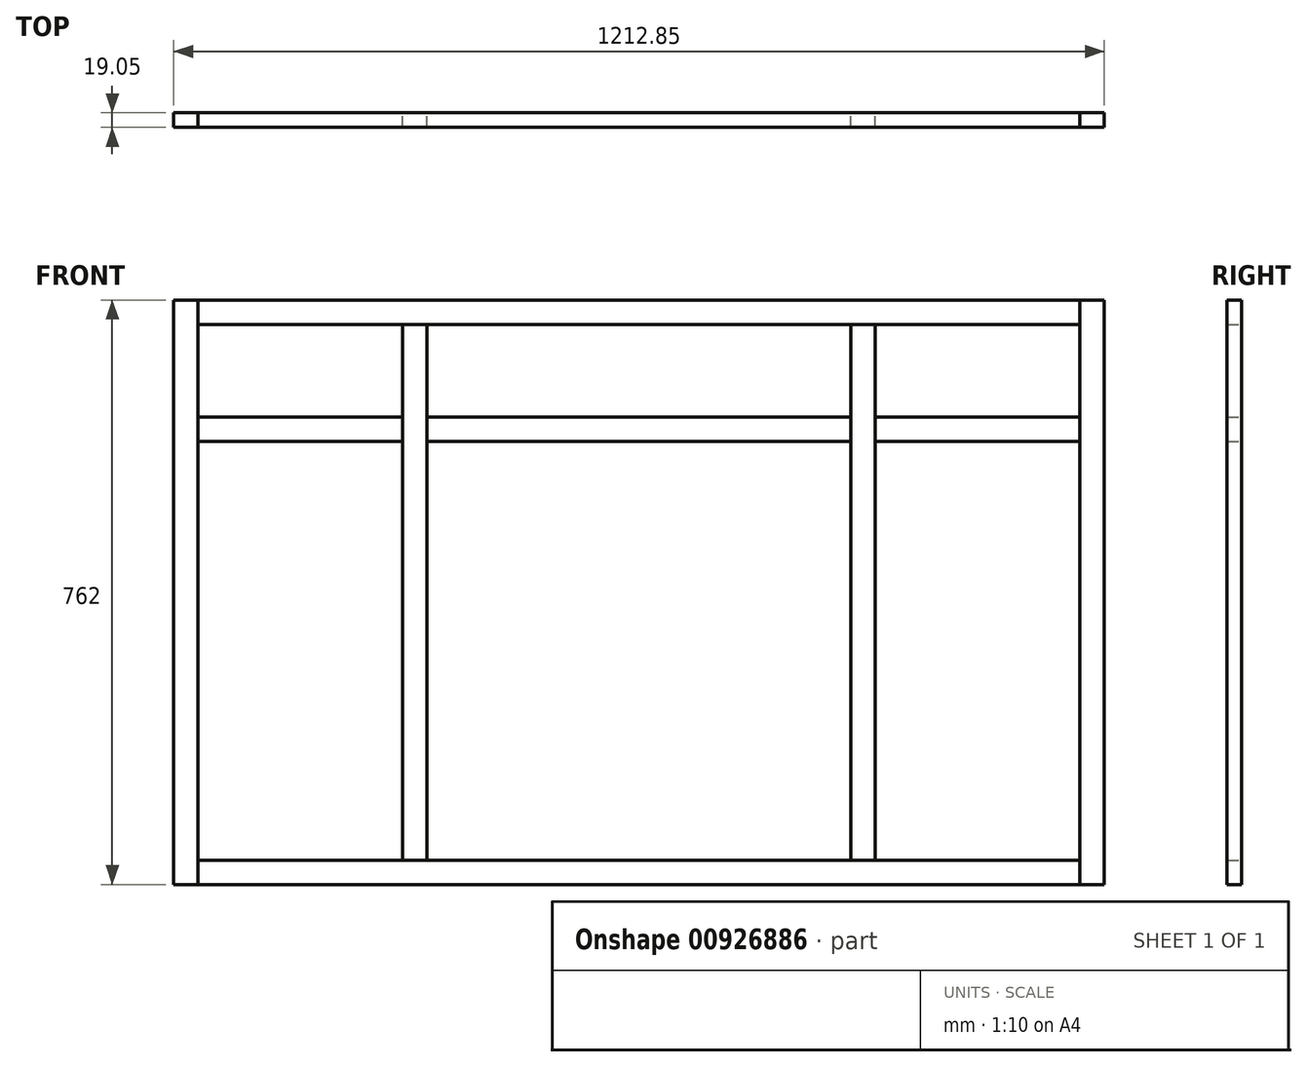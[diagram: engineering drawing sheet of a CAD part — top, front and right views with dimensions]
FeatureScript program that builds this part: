
annotation { "Feature Type Name" : "Feature", "Feature Type Description" : "" }
export const myFeature = defineFeature(function(context is Context, id is Id, definition is map)
    precondition{}
    {
        {
            var Q0;
            Q0=qCreatedBy(makeId("Front.planeOp"),FACE);
            var sketch = newSketch(context, id + "F0", { "sketchPlane" : qUnion([Q0])});
            skLineSegment(sketch, "E0.bottom", {"start": v(199.91, -224.24) * mm, "end": v(-130.29, -224.24) * mm});
            skLineSegment(sketch, "E0.top", {"start": v(199.91, 537.76) * mm, "end": v(-1012.94, 537.76) * mm});
            skLineSegment(sketch, "E0.left", {"start": v(199.91, -224.24) * mm, "end": v(199.91, 537.76) * mm});
            skLineSegment(sketch, "E0.right", {"start": v(-1012.94, -224.24) * mm, "end": v(-1012.94, 537.76) * mm});
            skLineSegment(sketch, "E1.0", {"start": v(168.16, 506.01) * mm, "end": v(-981.19, 506.01) * mm});
            skLineSegment(sketch, "E1.1", {"start": v(168.16, -192.49) * mm, "end": v(168.16, 506.01) * mm});
            skLineSegment(sketch, "E1.2", {"start": v(168.16, -192.49) * mm, "end": v(-98.54, -192.49) * mm});
            skLineSegment(sketch, "E1.3", {"start": v(-981.19, -192.49) * mm, "end": v(-981.19, 506.01) * mm});
            skLineSegment(sketch, "E2.0", {"start": v(-682.74, -192.49) * mm, "end": v(-682.74, 506.01) * mm});
            skLineSegment(sketch, "E3.0", {"start": v(-130.29, -192.49) * mm, "end": v(-130.29, 506.01) * mm});
            skLineSegment(sketch, "E4.0", {"start": v(-714.49, -192.49) * mm, "end": v(-714.49, 506.01) * mm});
            skLineSegment(sketch, "E5.0", {"start": v(-98.54, -192.49) * mm, "end": v(-98.54, 506.01) * mm});
            skLineSegment(sketch, "E6.0", {"start": v(168.16, 353.61) * mm, "end": v(-98.54, 353.61) * mm});
            skLineSegment(sketch, "E7.0", {"start": v(168.16, 385.36) * mm, "end": v(-98.54, 385.36) * mm});
            skLineSegment(sketch, "E8", {"start": v(-981.19, 506.01) * mm, "end": v(-981.19, 537.76) * mm});
            skLineSegment(sketch, "E9", {"start": v(-981.19, -192.49) * mm, "end": v(-981.19, -224.24) * mm});
            skLineSegment(sketch, "E10", {"start": v(168.16, -192.49) * mm, "end": v(168.16, -224.24) * mm});
            skLineSegment(sketch, "E11", {"start": v(168.16, 506.01) * mm, "end": v(168.16, 537.76) * mm});
            skLineSegment(sketch, "E12.trimOffspring", {"start": v(-714.49, 353.61) * mm, "end": v(-981.19, 353.61) * mm});
            skLineSegment(sketch, "E13.trimOffspring", {"start": v(-714.49, 385.36) * mm, "end": v(-981.19, 385.36) * mm});
            skLineSegment(sketch, "E14.trimOffspring", {"start": v(-130.29, 353.61) * mm, "end": v(-682.74, 353.61) * mm});
            skLineSegment(sketch, "E15.trimOffspring", {"start": v(-130.29, 385.36) * mm, "end": v(-682.74, 385.36) * mm});
            skLineSegment(sketch, "E16.trimOffspring", {"start": v(-682.74, -224.24) * mm, "end": v(-1012.94, -224.24) * mm});
            skLineSegment(sketch, "E17.trimOffspring", {"start": v(-714.49, -192.49) * mm, "end": v(-981.19, -192.49) * mm});
            skLineSegment(sketch, "E18", {"start": v(-682.74, -224.24) * mm, "end": v(-130.29, -224.24) * mm});
            skLineSegment(sketch, "E19", {"start": v(-682.74, -192.49) * mm, "end": v(-130.29, -192.49) * mm});
            skLineSegment(sketch, "E20", {"start": v(-714.49, -192.49) * mm, "end": v(-682.74, -192.49) * mm});
            skLineSegment(sketch, "E21", {"start": v(-130.29, -192.49) * mm, "end": v(-98.54, -192.49) * mm});
            skSolve(sketch);
        }
        {
            var Q0;
            {var subQ3=sQuery(id+"F0.wireOp",EDGE,"E0.right");Q0=makeQuery(id+"F0.imprint","IMPRINT",FACE,{"disambiguationData":[TD([[makeQuery(id+"F0.imprint","IMPRINT",EDGE,{"derivedFrom":subQ3}),-1.0]])]});}
            var Q1;
            {var subQ6=sQuery(id+"F0.wireOp",EDGE,"E20");Q1=makeQuery(id+"F0.imprint","IMPRINT",FACE,{"disambiguationData":[TD([[makeQuery(id+"F0.imprint","IMPRINT",EDGE,{"derivedFrom":subQ6}),1.0]])]});}
            var Q2;
            {var subQ4=sQuery(id+"F0.wireOp",EDGE,"E21");Q2=makeQuery(id+"F0.imprint","IMPRINT",FACE,{"disambiguationData":[TD([[makeQuery(id+"F0.imprint","IMPRINT",EDGE,{"derivedFrom":subQ4}),1.0]])]});}
            var Q3;
            {var subQ3=sQuery(id+"F0.wireOp",EDGE,"E0.left");Q3=makeQuery(id+"F0.imprint","IMPRINT",FACE,{"disambiguationData":[TD([[makeQuery(id+"F0.imprint","IMPRINT",EDGE,{"derivedFrom":subQ3}),1.0]])]});}
            extrude(context, id + "F1", {"entities" : qUnion([Q0, Q1, Q2, Q3]), "depth" : 19.05 * mm, "offsetDistance" : 25.4 * mm});
        }
        {
            var Q0;
            {var subQ5=sQuery(id+"F0.wireOp",EDGE,"E8");Q0=makeQuery(id+"F0.imprint","IMPRINT",FACE,{"disambiguationData":[TD([[makeQuery(id+"F0.imprint","IMPRINT",EDGE,{"derivedFrom":subQ5}),-1.0]])]});}
            var Q1;
            {var subQ0=sQuery(id+"F0.wireOp",EDGE,"E12.trimOffspring");Q1=makeQuery(id+"F0.imprint","IMPRINT",FACE,{"disambiguationData":[TD([[makeQuery(id+"F0.imprint","IMPRINT",EDGE,{"derivedFrom":subQ0}),-1.0]])]});}
            var Q2;
            {var subQ0=sQuery(id+"F0.wireOp",EDGE,"E14.trimOffspring");Q2=makeQuery(id+"F0.imprint","IMPRINT",FACE,{"disambiguationData":[TD([[makeQuery(id+"F0.imprint","IMPRINT",EDGE,{"derivedFrom":subQ0}),-1.0]])]});}
            var Q3;
            {var subQ0=sQuery(id+"F0.wireOp",EDGE,"E6.0");Q3=makeQuery(id+"F0.imprint","IMPRINT",FACE,{"disambiguationData":[TD([[makeQuery(id+"F0.imprint","IMPRINT",EDGE,{"derivedFrom":subQ0}),-1.0]])]});}
            var Q4;
            Q4=makeQuery(id+"F0.imprint","IMPRINT",FACE,{"disambiguationData":[TD([[makeQuery(id+"F0.imprint","IMPRINT",EDGE,{"derivedFrom":sQuery(id+"F0.wireOp",EDGE,"E1.2")}),1.0]])]});
            extrude(context, id + "F2", {"entities" : qUnion([Q0, Q1, Q2, Q3, Q4]), "depth" : 19.05 * mm, "offsetDistance" : 25.4 * mm});
        }
    });
